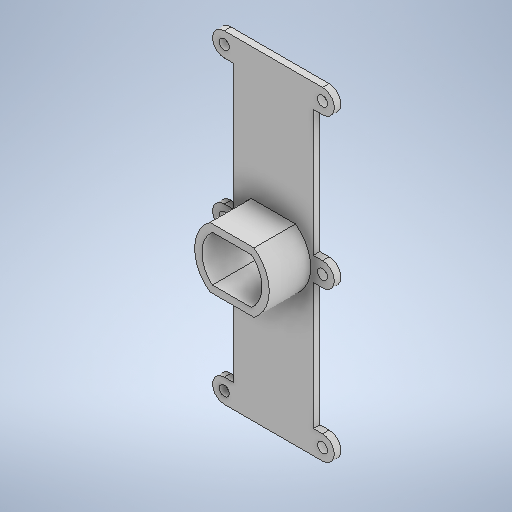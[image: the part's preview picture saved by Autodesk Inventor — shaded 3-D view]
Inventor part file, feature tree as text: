
AUTODESK INVENTOR PART (.ipt)
format: ipt  version: 2025.1 (Build 291241000, 241)  size: 304,640 bytes
history: native  units: mm
features: extrude x2, sketch x1, plane x1
ambient origin geometry x8: Origin, YZ Plane, XZ Plane, XY Plane, X Axis, Y Axis, Z Axis, Center Point
bodies: Solid1 (feature_tree)
feature tree (4):
  sketch  "Sketch1"  dims[d0=24.3mm d1=19.0mm d2=4.2mm d3=4.9mm d4=134.5mm d5=4.2mm d6=4.9mm d7=2.75mm d8=0.0mm d9=3.0mm d10=20.0mm d11=0.0mm d12=50.0mm d34=33.2mm d35=3.8mm d36=3.8mm d37=12.5mm d38=12.5mm d31=0.5mm d32=0.872665mm d33=0.5mm]
  extrude  "Extrusion1"  Depth=12.5mm
  extrude  "Extrusion2"  Depth=4.9mm
  plane  "Work Plane1"
